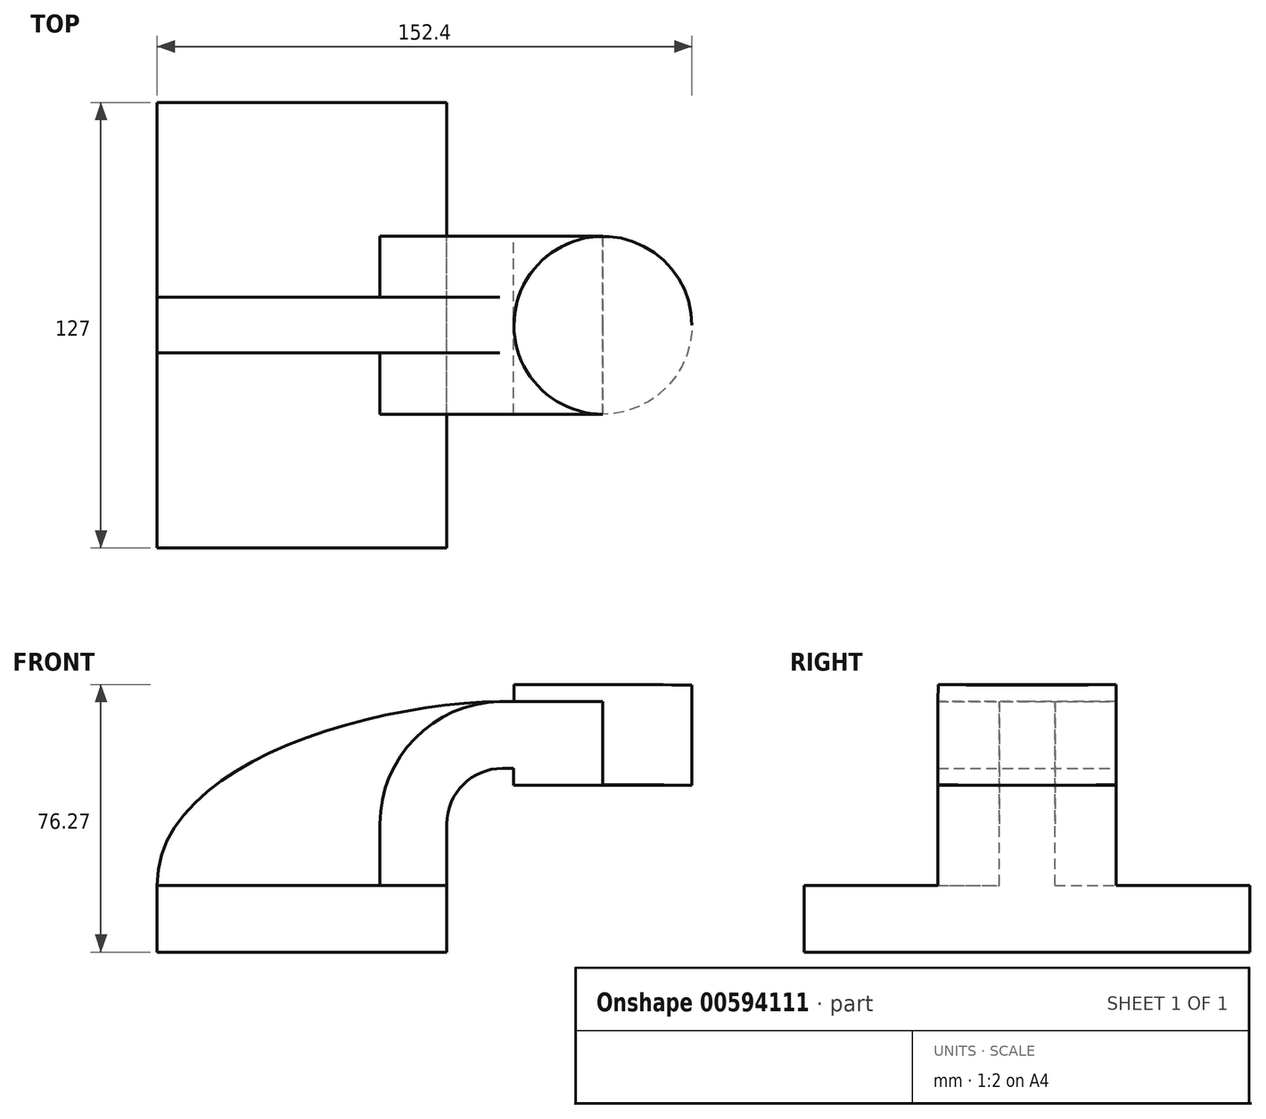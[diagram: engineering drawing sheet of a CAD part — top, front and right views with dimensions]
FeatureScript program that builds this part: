
annotation { "Feature Type Name" : "Feature", "Feature Type Description" : "" }
export const myFeature = defineFeature(function(context is Context, id is Id, definition is map)
    precondition{}
    {
        {
            var Q0;
            Q0=qCreatedBy(makeId("Front.planeOp"),FACE);
            var sketch = newSketch(context, id + "F0", { "sketchPlane" : qUnion([Q0])});
            skLineSegment(sketch, "E0.bottom", {"start": v(-39.75, 9.52) * mm, "end": v(42.8, 9.53) * mm});
            skLineSegment(sketch, "E0.top", {"start": v(-39.75, -9.53) * mm, "end": v(42.8, -9.52) * mm});
            skLineSegment(sketch, "E0.left", {"start": v(-39.75, 9.52) * mm, "end": v(-39.75, -9.53) * mm});
            skLineSegment(sketch, "E0.right", {"start": v(42.8, 9.53) * mm, "end": v(42.8, -9.52) * mm});
            skPoint(sketch, "E0.middle", {"position": v(1.52, 0) * mm});
            skLineSegment(sketch, "E1.bottom", {"start": v(112.65, 66.68) * mm, "end": v(61.85, 66.68) * mm});
            skLineSegment(sketch, "E1.top", {"start": v(112.65, 38.1) * mm, "end": v(61.85, 38.1) * mm});
            skLineSegment(sketch, "E1.left", {"start": v(112.65, 66.68) * mm, "end": v(112.65, 38.1) * mm});
            skLineSegment(sketch, "E1.right", {"start": v(61.85, 66.68) * mm, "end": v(61.85, 38.1) * mm});
            skPoint(sketch, "E1.middle", {"position": v(87.25, 52.39) * mm});
            skLineSegment(sketch, "E2", {"start": v(42.8, 9.53) * mm, "end": v(42.8, 27) * mm});
            skArc(sketch, "E3", {"start": v(42.8, 27) * mm, "mid": v(47.45, 38.23) * mm, "end": v(58.67, 42.88) * mm});
            skLineSegment(sketch, "E4", {"start": v(58.67, 42.88) * mm, "end": v(86.88, 42.88) * mm});
            skLineSegment(sketch, "E5.0", {"start": v(58.67, 61.93) * mm, "end": v(87.29, 61.93) * mm});
            skArc(sketch, "E5.1", {"start": v(23.75, 27) * mm, "mid": v(33.98, 51.7) * mm, "end": v(58.67, 61.93) * mm});
            skLineSegment(sketch, "E5.2", {"start": v(23.75, 9.53) * mm, "end": v(23.75, 27) * mm});
            skLineSegment(sketch, "E6", {"start": v(87.25, 38.1) * mm, "end": v(87.29, 66.68) * mm});
            skFitSpline(sketch, "E7", {"points": [v(-39.75, 9.52) * mm, v(58.67, 61.93) * mm], "startDerivative": vector(-0.76, 103.94) * mm, "endDerivative": vector(112.33, 0.86) * mm});
            skSolve(sketch);
        }
        {
            var Q0;
            Q0=makeQuery(id+"F0.imprint","IMPRINT",FACE,{"disambiguationData":[TD([[makeQuery(id+"F0.imprint","IMPRINT",EDGE,{"derivedFrom":sQuery(id+"F0.wireOp",EDGE,"E0.top")}),1.0]])]});
            extrude(context, id + "F1", {"entities" : qUnion([Q0]), "endBound" : BoundingType.SYMMETRIC, "depth" : 127 * mm, "offsetDistance" : 25.4 * mm});
        }
        {
            var Q0;
            {var subQ1=sQuery(id+"F0.wireOp",EDGE,"E2");Q0=makeQuery(id+"F0.imprint","IMPRINT",FACE,{"disambiguationData":[TD([[makeQuery(id+"F0.imprint","IMPRINT",EDGE,{"derivedFrom":subQ1}),1.0]])]});}
            extrude(context, id + "F2", {"entities" : qUnion([Q0]), "operationType" : NewBodyOperationType.ADD, "endBound" : BoundingType.SYMMETRIC, "depth" : 50.8 * mm, "offsetDistance" : 25.4 * mm});
        }
        {
            var Q0;
            {var subQ1=sQuery(id+"F0.wireOp",EDGE,"E1.right");var subQ5=sQuery(id+"F0.wireOp",EDGE,"E1.top");var subQ6=makeQuery(id+"F0.imprint","INTERSECT",VERTEX,{"derivedFrom":[subQ5,subQ1]});Q0=makeQuery(id+"F0.imprint","IMPRINT",FACE,{"disambiguationData":[TD([[makeQuery(id+"F0.imprint","IMPRINT",EDGE,{"disambiguationData":[TD([[subQ6,1.0]])],"derivedFrom":subQ5}),-1.0]])]});}
            extrude(context, id + "F3", {"entities" : qUnion([Q0]), "operationType" : NewBodyOperationType.ADD, "endBound" : BoundingType.SYMMETRIC, "depth" : 50.8 * mm, "offsetDistance" : 25.4 * mm});
        }
        {
            var Q0;
            {var subQ3=sQuery(id+"F0.wireOp",EDGE,"E5.2");Q0=makeQuery(id+"F0.imprint","IMPRINT",FACE,{"disambiguationData":[TD([[makeQuery(id+"F0.imprint","IMPRINT",EDGE,{"derivedFrom":subQ3}),1.0]])]});}
            extrude(context, id + "F4", {"entities" : qUnion([Q0]), "operationType" : NewBodyOperationType.ADD, "endBound" : BoundingType.SYMMETRIC, "depth" : 15.88 * mm, "offsetDistance" : 25.4 * mm});
        }
        {
            var Q0;
            {var subQ4=sQuery(id+"F0.wireOp",EDGE,"E1.left");Q0=makeQuery(id+"F0.imprint","IMPRINT",FACE,{"disambiguationData":[TD([[makeQuery(id+"F0.imprint","IMPRINT",EDGE,{"derivedFrom":subQ4}),-1.0]])]});}
            var Q1;
            Q1=sQuery(id+"F0.wireOp",EDGE,"E6");
            revolve(context, id + "F5", {"operationType" : NewBodyOperationType.ADD, "entities" : qUnion([Q0]), "axis" : qUnion([Q1]), "revolveType" : RevolveType.FULL});
        }
    });
